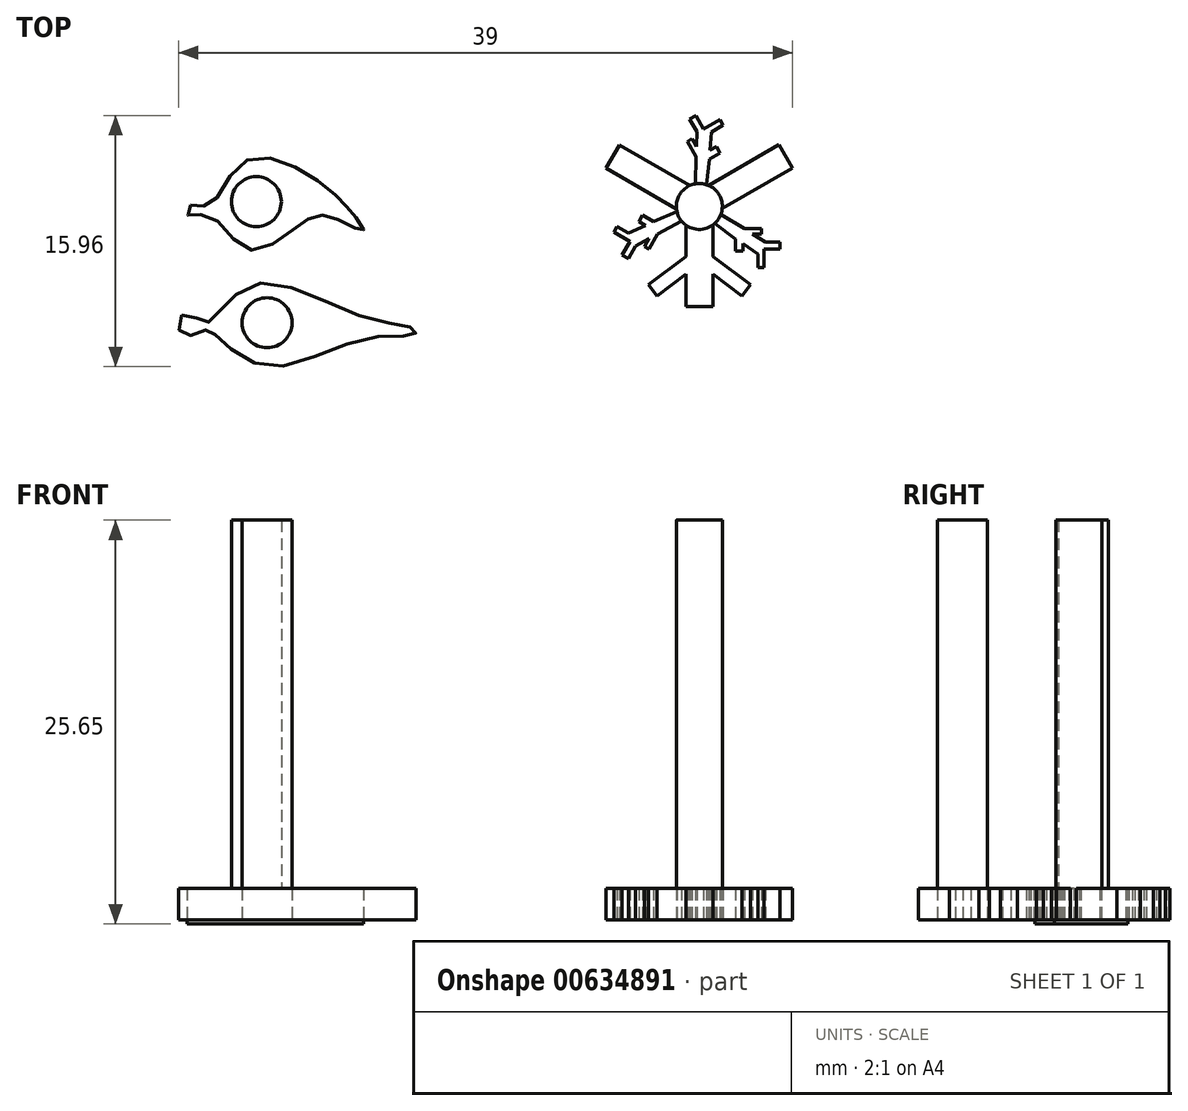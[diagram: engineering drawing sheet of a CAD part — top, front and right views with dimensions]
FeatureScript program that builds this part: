
annotation { "Feature Type Name" : "Feature", "Feature Type Description" : "" }
export const myFeature = defineFeature(function(context is Context, id is Id, definition is map)
    precondition{}
    {
        {
            var Q0;
            Q0=qCreatedBy(makeId("Top.planeOp"),FACE);
            var sketch = newSketch(context, id + "F0", { "sketchPlane" : qUnion([Q0])});
            skLineSegment(sketch, "E0.bottom", {"start": v(-0.85, 0) * mm, "end": v(0.86, 0) * mm});
            skLineSegment(sketch, "E0.top", {"start": v(-0.85, -6.35) * mm, "end": v(0.86, -6.35) * mm});
            skLineSegment(sketch, "E0.left", {"start": v(-0.85, 0) * mm, "end": v(-0.85, -6.35) * mm});
            skLineSegment(sketch, "E0.right", {"start": v(0.86, 0) * mm, "end": v(0.86, -6.35) * mm});
            skLineSegment(sketch, "E1", {"start": v(-0.85, -3.17) * mm, "end": v(-3.24, -4.96) * mm});
            skLineSegment(sketch, "E2", {"start": v(-3.24, -4.96) * mm, "end": v(-2.7, -5.69) * mm});
            skLineSegment(sketch, "E3", {"start": v(-2.7, -5.69) * mm, "end": v(-0.85, -4.3) * mm});
            skLineSegment(sketch, "E4", {"start": v(-0.85, -4.3) * mm, "end": v(-0.85, -3.17) * mm});
            skLineSegment(sketch, "E5", {"start": v(0, 0) * mm, "end": v(0, -6.35) * mm, "construction": true});
            skLineSegment(sketch, "E6.MirrorCS", {"start": v(2.71, -5.69) * mm, "end": v(0.86, -4.3) * mm});
            skLineSegment(sketch, "E7.MirrorCS", {"start": v(3.25, -4.96) * mm, "end": v(2.71, -5.69) * mm});
            skLineSegment(sketch, "E8.MirrorCS", {"start": v(0.86, -3.17) * mm, "end": v(3.25, -4.96) * mm});
            skLineSegment(sketch, "E9.MirrorCS", {"start": v(0.86, -4.3) * mm, "end": v(0.86, -3.17) * mm});
            skLineSegment(sketch, "E10.MirrorCS", {"start": v(0.86, 0) * mm, "end": v(-0.85, 0) * mm});
            skLineSegment(sketch, "E11.MirrorCS", {"start": v(0.86, -6.35) * mm, "end": v(-0.85, -6.35) * mm});
            skLineSegment(sketch, "E12", {"start": v(-0.45, 0) * mm, "end": v(2.29, -2.06) * mm});
            skLineSegment(sketch, "E13", {"start": v(2.29, -2.06) * mm, "end": v(2.29, -2.84) * mm});
            skLineSegment(sketch, "E14", {"start": v(2.29, -2.84) * mm, "end": v(2.76, -2.84) * mm});
            skLineSegment(sketch, "E15", {"start": v(2.76, -2.84) * mm, "end": v(2.76, -2.37) * mm});
            skLineSegment(sketch, "E16", {"start": v(2.76, -2.37) * mm, "end": v(3.71, -3.03) * mm});
            skLineSegment(sketch, "E17", {"start": v(3.71, -3.03) * mm, "end": v(3.71, -3.9) * mm});
            skLineSegment(sketch, "E18", {"start": v(3.71, -3.9) * mm, "end": v(4.12, -3.9) * mm});
            skLineSegment(sketch, "E19", {"start": v(4.12, -3.9) * mm, "end": v(4.12, -2.7) * mm});
            skLineSegment(sketch, "E20", {"start": v(4.12, -2.7) * mm, "end": v(5.12, -2.7) * mm});
            skLineSegment(sketch, "E21", {"start": v(5.12, -2.7) * mm, "end": v(5.12, -2.25) * mm});
            skLineSegment(sketch, "E22", {"start": v(5.12, -2.25) * mm, "end": v(4.2, -2.25) * mm});
            skLineSegment(sketch, "E23", {"start": v(4.2, -2.25) * mm, "end": v(3.38, -1.75) * mm});
            skLineSegment(sketch, "E24", {"start": v(3.38, -1.75) * mm, "end": v(3.95, -1.75) * mm});
            skLineSegment(sketch, "E25", {"start": v(3.95, -1.75) * mm, "end": v(3.95, -1.41) * mm});
            skLineSegment(sketch, "E26", {"start": v(3.95, -1.41) * mm, "end": v(2.86, -1.41) * mm});
            skLineSegment(sketch, "E27", {"start": v(2.86, -1.41) * mm, "end": v(0.5, 0) * mm});
            skLineSegment(sketch, "E28", {"start": v(0.5, 0) * mm, "end": v(-0.45, 0) * mm});
            skLineSegment(sketch, "E29.1.0", {"start": v(-0.75, 4.13) * mm, "end": v(-0.2, 3.18) * mm});
            skLineSegment(sketch, "E29.1.1", {"start": v(2.32, 2.34) * mm, "end": v(2.67, 5.3) * mm});
            skLineSegment(sketch, "E29.1.2", {"start": v(0, 0) * mm, "end": v(5.5, 3.18) * mm, "construction": true});
            skLineSegment(sketch, "E29.1.3", {"start": v(0.43, -0.74) * mm, "end": v(5.92, 2.44) * mm});
            skLineSegment(sketch, "E29.1.4", {"start": v(0.67, 3.57) * mm, "end": v(0.77, 4.73) * mm});
            skLineSegment(sketch, "E29.1.5", {"start": v(-0.61, 5.56) * mm, "end": v(-0.15, 4.75) * mm});
            skLineSegment(sketch, "E29.1.6", {"start": v(3.57, 5.2) * mm, "end": v(3.3, 2.9) * mm});
            skLineSegment(sketch, "E29.1.7", {"start": v(-0.43, 0.75) * mm, "end": v(5.07, 3.92) * mm});
            skLineSegment(sketch, "E29.1.8", {"start": v(3.3, 2.9) * mm, "end": v(2.32, 2.34) * mm});
            skLineSegment(sketch, "E29.1.9", {"start": v(-0.15, 4.75) * mm, "end": v(-0.18, 3.8) * mm});
            skLineSegment(sketch, "E29.1.10", {"start": v(0.28, 4.92) * mm, "end": v(-0.22, 5.78) * mm});
            skLineSegment(sketch, "E29.1.11", {"start": v(5.92, -0.33) * mm, "end": v(6.27, 0.5) * mm});
            skLineSegment(sketch, "E29.1.12", {"start": v(0.77, 4.73) * mm, "end": v(1.51, 5.16) * mm});
            skLineSegment(sketch, "E29.1.13", {"start": v(0.64, 3) * mm, "end": v(1.32, 3.4) * mm});
            skLineSegment(sketch, "E29.1.14", {"start": v(2.67, 5.3) * mm, "end": v(3.57, 5.2) * mm});
            skLineSegment(sketch, "E29.1.15", {"start": v(6.27, 0.5) * mm, "end": v(4.15, 1.41) * mm});
            skLineSegment(sketch, "E29.1.16", {"start": v(-0.2, 3.18) * mm, "end": v(-0.25, 0.43) * mm});
            skLineSegment(sketch, "E29.1.17", {"start": v(5.92, 2.44) * mm, "end": v(5.07, 3.92) * mm});
            skLineSegment(sketch, "E29.1.18", {"start": v(1.3, 5.51) * mm, "end": v(0.28, 4.92) * mm});
            skLineSegment(sketch, "E29.1.19", {"start": v(3.18, 0.85) * mm, "end": v(5.92, -0.33) * mm});
            skLineSegment(sketch, "E29.1.20", {"start": v(0.23, -0.4) * mm, "end": v(0.64, 3) * mm});
            skLineSegment(sketch, "E29.1.21", {"start": v(2.32, 2.34) * mm, "end": v(2.67, 5.3) * mm});
            skLineSegment(sketch, "E29.1.22", {"start": v(2.67, 5.3) * mm, "end": v(3.57, 5.2) * mm});
            skLineSegment(sketch, "E29.1.23", {"start": v(-0.43, 0.75) * mm, "end": v(5.07, 3.92) * mm});
            skLineSegment(sketch, "E29.1.24", {"start": v(0.43, -0.74) * mm, "end": v(5.92, 2.44) * mm});
            skLineSegment(sketch, "E29.1.25", {"start": v(6.27, 0.5) * mm, "end": v(4.15, 1.41) * mm});
            skLineSegment(sketch, "E29.1.26", {"start": v(5.07, 3.92) * mm, "end": v(5.92, 2.44) * mm});
            skLineSegment(sketch, "E29.1.27", {"start": v(5.92, -0.33) * mm, "end": v(6.27, 0.5) * mm});
            skLineSegment(sketch, "E29.1.28", {"start": v(4.15, 1.41) * mm, "end": v(3.18, 0.85) * mm});
            skLineSegment(sketch, "E29.1.29", {"start": v(3.57, 5.2) * mm, "end": v(3.3, 2.9) * mm});
            skLineSegment(sketch, "E29.1.30", {"start": v(-0.25, 0.43) * mm, "end": v(0.23, -0.4) * mm});
            skLineSegment(sketch, "E29.1.31", {"start": v(3.3, 2.9) * mm, "end": v(2.32, 2.34) * mm});
            skLineSegment(sketch, "E29.1.32", {"start": v(3.18, 0.85) * mm, "end": v(5.92, -0.33) * mm});
            skLineSegment(sketch, "E29.1.33", {"start": v(-0.18, 3.8) * mm, "end": v(-0.46, 4.3) * mm});
            skLineSegment(sketch, "E29.1.34", {"start": v(4.15, 1.41) * mm, "end": v(3.18, 0.85) * mm});
            skLineSegment(sketch, "E29.1.35", {"start": v(1.51, 5.16) * mm, "end": v(1.3, 5.51) * mm});
            skLineSegment(sketch, "E29.1.36", {"start": v(-0.22, 5.78) * mm, "end": v(-0.61, 5.56) * mm});
            skLineSegment(sketch, "E29.1.37", {"start": v(1.08, 3.81) * mm, "end": v(0.67, 3.57) * mm});
            skLineSegment(sketch, "E29.1.38", {"start": v(0.43, -0.74) * mm, "end": v(-0.43, 0.75) * mm});
            skLineSegment(sketch, "E29.1.39", {"start": v(-0.46, 4.3) * mm, "end": v(-0.75, 4.13) * mm});
            skLineSegment(sketch, "E29.1.40", {"start": v(1.32, 3.4) * mm, "end": v(1.08, 3.81) * mm});
            skLineSegment(sketch, "E29.1.41", {"start": v(-0.43, 0.75) * mm, "end": v(0.43, -0.74) * mm});
            skLineSegment(sketch, "E29.2.0", {"start": v(-3.2, -2.72) * mm, "end": v(-2.65, -1.77) * mm});
            skLineSegment(sketch, "E29.2.1", {"start": v(-3.18, 0.84) * mm, "end": v(-5.93, -0.34) * mm});
            skLineSegment(sketch, "E29.2.2", {"start": v(0, 0) * mm, "end": v(-5.5, 3.17) * mm, "construction": true});
            skLineSegment(sketch, "E29.2.3", {"start": v(0.43, 0.74) * mm, "end": v(-5.07, 3.91) * mm});
            skLineSegment(sketch, "E29.2.4", {"start": v(-3.43, -1.2) * mm, "end": v(-4.48, -1.7) * mm});
            skLineSegment(sketch, "E29.2.5", {"start": v(-4.5, -3.3) * mm, "end": v(-4.04, -2.5) * mm});
            skLineSegment(sketch, "E29.2.6", {"start": v(-6.28, 0.5) * mm, "end": v(-4.16, 1.4) * mm});
            skLineSegment(sketch, "E29.2.7", {"start": v(-0.43, -0.75) * mm, "end": v(-5.93, 2.43) * mm});
            skLineSegment(sketch, "E29.2.8", {"start": v(-4.16, 1.4) * mm, "end": v(-3.18, 0.84) * mm});
            skLineSegment(sketch, "E29.2.9", {"start": v(-4.04, -2.5) * mm, "end": v(-3.2, -2.05) * mm});
            skLineSegment(sketch, "E29.2.10", {"start": v(-4.4, -2.22) * mm, "end": v(-4.9, -3.08) * mm});
            skLineSegment(sketch, "E29.2.11", {"start": v(-2.68, 5.29) * mm, "end": v(-3.57, 5.18) * mm});
            skLineSegment(sketch, "E29.2.12", {"start": v(-4.48, -1.7) * mm, "end": v(-5.23, -1.27) * mm});
            skLineSegment(sketch, "E29.2.13", {"start": v(-2.92, -0.95) * mm, "end": v(-3.6, -0.56) * mm});
            skLineSegment(sketch, "E29.2.14", {"start": v(-5.93, -0.34) * mm, "end": v(-6.28, 0.5) * mm});
            skLineSegment(sketch, "E29.2.15", {"start": v(-3.57, 5.18) * mm, "end": v(-3.3, 2.89) * mm});
            skLineSegment(sketch, "E29.2.16", {"start": v(-2.65, -1.77) * mm, "end": v(-0.25, -0.43) * mm});
            skLineSegment(sketch, "E29.2.17", {"start": v(-5.07, 3.91) * mm, "end": v(-5.93, 2.43) * mm});
            skLineSegment(sketch, "E29.2.18", {"start": v(-5.43, -1.62) * mm, "end": v(-4.4, -2.22) * mm});
            skLineSegment(sketch, "E29.2.19", {"start": v(-2.32, 2.32) * mm, "end": v(-2.68, 5.29) * mm});
            skLineSegment(sketch, "E29.2.20", {"start": v(0.23, 0.4) * mm, "end": v(-2.92, -0.95) * mm});
            skLineSegment(sketch, "E29.2.21", {"start": v(-3.18, 0.84) * mm, "end": v(-5.93, -0.34) * mm});
            skLineSegment(sketch, "E29.2.22", {"start": v(-5.93, -0.34) * mm, "end": v(-6.28, 0.5) * mm});
            skLineSegment(sketch, "E29.2.23", {"start": v(-0.43, -0.75) * mm, "end": v(-5.93, 2.43) * mm});
            skLineSegment(sketch, "E29.2.24", {"start": v(0.43, 0.74) * mm, "end": v(-5.07, 3.91) * mm});
            skLineSegment(sketch, "E29.2.25", {"start": v(-3.57, 5.18) * mm, "end": v(-3.3, 2.89) * mm});
            skLineSegment(sketch, "E29.2.26", {"start": v(-5.93, 2.43) * mm, "end": v(-5.07, 3.91) * mm});
            skLineSegment(sketch, "E29.2.27", {"start": v(-2.68, 5.29) * mm, "end": v(-3.57, 5.18) * mm});
            skLineSegment(sketch, "E29.2.28", {"start": v(-3.3, 2.89) * mm, "end": v(-2.32, 2.32) * mm});
            skLineSegment(sketch, "E29.2.29", {"start": v(-6.28, 0.5) * mm, "end": v(-4.16, 1.4) * mm});
            skLineSegment(sketch, "E29.2.30", {"start": v(-0.25, -0.43) * mm, "end": v(0.23, 0.4) * mm});
            skLineSegment(sketch, "E29.2.31", {"start": v(-4.16, 1.4) * mm, "end": v(-3.18, 0.84) * mm});
            skLineSegment(sketch, "E29.2.32", {"start": v(-2.32, 2.32) * mm, "end": v(-2.68, 5.29) * mm});
            skLineSegment(sketch, "E29.2.33", {"start": v(-3.2, -2.05) * mm, "end": v(-3.49, -2.55) * mm});
            skLineSegment(sketch, "E29.2.34", {"start": v(-3.3, 2.89) * mm, "end": v(-2.32, 2.32) * mm});
            skLineSegment(sketch, "E29.2.35", {"start": v(-5.23, -1.27) * mm, "end": v(-5.43, -1.62) * mm});
            skLineSegment(sketch, "E29.2.36", {"start": v(-4.9, -3.08) * mm, "end": v(-4.5, -3.3) * mm});
            skLineSegment(sketch, "E29.2.37", {"start": v(-3.84, -0.97) * mm, "end": v(-3.43, -1.2) * mm});
            skLineSegment(sketch, "E29.2.38", {"start": v(0.43, 0.74) * mm, "end": v(-0.43, -0.75) * mm});
            skLineSegment(sketch, "E29.2.39", {"start": v(-3.49, -2.55) * mm, "end": v(-3.2, -2.72) * mm});
            skLineSegment(sketch, "E29.2.40", {"start": v(-3.6, -0.56) * mm, "end": v(-3.84, -0.97) * mm});
            skLineSegment(sketch, "E29.2.41", {"start": v(-0.43, -0.75) * mm, "end": v(0.43, 0.74) * mm});
            skPoint(sketch, "E29.center", {"position": v(0, 0) * mm});
            skSolve(sketch);
        }
        {
            var Q0;
            Q0=qCreatedBy(makeId("Top.planeOp"),FACE);
            var sketch = newSketch(context, id + "F1", { "sketchPlane" : qUnion([Q0])});
            skCircle(sketch, "E30", {"center": v(0, 0) * mm, "radius": 1.46 * mm});
            skSolve(sketch);
        }
        {
            var Q0;
            {var subQ9=sQuery(id+"F0.wireOp",EDGE,"032354c9-7b22-4bc2-b53b-3968bda45a61.1.0");Q0=makeQuery(id+"F0.imprint","IMPRINT",FACE,{"disambiguationData":[TD([[makeQuery(id+"F0.imprint","IMPRINT",EDGE,{"derivedFrom":subQ9}),1.0]])]});}
            var Q1;
            {var subQ9=sQuery(id+"F0.wireOp",EDGE,"032354c9-7b22-4bc2-b53b-3968bda45a61.2.0");Q1=makeQuery(id+"F0.imprint","IMPRINT",FACE,{"disambiguationData":[TD([[makeQuery(id+"F0.imprint","IMPRINT",EDGE,{"derivedFrom":subQ9}),1.0]])]});}
            var Q2;
            {var subQ8=sQuery(id+"F0.wireOp",EDGE,"032354c9-7b22-4bc2-b53b-3968bda45a61.1.30");Q2=makeQuery(id+"F0.imprint","IMPRINT",FACE,{"disambiguationData":[TD([[makeQuery(id+"F0.imprint","IMPRINT",EDGE,{"derivedFrom":subQ8}),-1.0]])]});}
            var Q3;
            {var subQ10=sQuery(id+"F0.wireOp",EDGE,"E11.MirrorCS");Q3=makeQuery(id+"F0.imprint","IMPRINT",FACE,{"disambiguationData":[TD([[makeQuery(id+"F0.imprint","IMPRINT",EDGE,{"derivedFrom":subQ10}),-1.0]])]});}
            var Q4;
            {var subQ0=sQuery(id+"F0.wireOp",EDGE,"E1");Q4=makeQuery(id+"F0.imprint","IMPRINT",FACE,{"disambiguationData":[TD([[makeQuery(id+"F0.imprint","IMPRINT",EDGE,{"derivedFrom":subQ0}),1.0]])]});}
            var Q5;
            Q5=makeQuery(id+"F0.imprint","IMPRINT",FACE,{"disambiguationData":[TD([[makeQuery(id+"F0.imprint","IMPRINT",EDGE,{"derivedFrom":sQuery(id+"F0.wireOp",EDGE,"E8.MirrorCS")}),-1.0]])]});
            var Q6;
            {var subQ0=sQuery(id+"F0.wireOp",EDGE,"D4slwSDG-l3qi-5vr4-5RfH-pFX6ATX0QrVD");Q6=makeQuery(id+"F0.imprint","IMPRINT",FACE,{"disambiguationData":[TD([[makeQuery(id+"F0.imprint","IMPRINT",EDGE,{"derivedFrom":subQ0}),1.0]])]});}
            var Q7;
            {var subQ1=sQuery(id+"F0.wireOp",EDGE,"98ac017a-216a-4e28-945e-33d32b6503b70.MirrorCS");Q7=makeQuery(id+"F0.imprint","IMPRINT",FACE,{"disambiguationData":[TD([[makeQuery(id+"F0.imprint","IMPRINT",EDGE,{"derivedFrom":subQ1}),-1.0]])]});}
            var Q8;
            {var subQ0=sQuery(id+"F0.wireOp",EDGE,"032354c9-7b22-4bc2-b53b-3968bda45a61.1.3");Q8=makeQuery(id+"F0.imprint","IMPRINT",FACE,{"disambiguationData":[TD([[makeQuery(id+"F0.imprint","IMPRINT",EDGE,{"derivedFrom":subQ0}),1.0]])]});}
            var Q9;
            {var subQ1=sQuery(id+"F0.wireOp",EDGE,"032354c9-7b22-4bc2-b53b-3968bda45a61.1.10");Q9=makeQuery(id+"F0.imprint","IMPRINT",FACE,{"disambiguationData":[TD([[makeQuery(id+"F0.imprint","IMPRINT",EDGE,{"derivedFrom":subQ1}),-1.0]])]});}
            var Q10;
            Q10=makeQuery(id+"F0.imprint","IMPRINT",FACE,{"disambiguationData":[TD([[makeQuery(id+"F0.imprint","IMPRINT",EDGE,{"derivedFrom":sQuery(id+"F0.wireOp",EDGE,"032354c9-7b22-4bc2-b53b-3968bda45a61.1.23")}),1.0]])]});
            var Q11;
            Q11=makeQuery(id+"F0.imprint","IMPRINT",FACE,{"disambiguationData":[TD([[makeQuery(id+"F0.imprint","IMPRINT",EDGE,{"derivedFrom":sQuery(id+"F0.wireOp",EDGE,"032354c9-7b22-4bc2-b53b-3968bda45a61.1.24")}),-1.0]])]});
            var Q12;
            {var subQ0=sQuery(id+"F0.wireOp",EDGE,"032354c9-7b22-4bc2-b53b-3968bda45a61.2.3");Q12=makeQuery(id+"F0.imprint","IMPRINT",FACE,{"disambiguationData":[TD([[makeQuery(id+"F0.imprint","IMPRINT",EDGE,{"derivedFrom":subQ0}),1.0]])]});}
            var Q13;
            {var subQ1=sQuery(id+"F0.wireOp",EDGE,"032354c9-7b22-4bc2-b53b-3968bda45a61.2.10");Q13=makeQuery(id+"F0.imprint","IMPRINT",FACE,{"disambiguationData":[TD([[makeQuery(id+"F0.imprint","IMPRINT",EDGE,{"derivedFrom":subQ1}),-1.0]])]});}
            var Q14;
            Q14=makeQuery(id+"F0.imprint","IMPRINT",FACE,{"disambiguationData":[TD([[makeQuery(id+"F0.imprint","IMPRINT",EDGE,{"derivedFrom":sQuery(id+"F0.wireOp",EDGE,"032354c9-7b22-4bc2-b53b-3968bda45a61.2.23")}),1.0]])]});
            var Q15;
            Q15=makeQuery(id+"F0.imprint","IMPRINT",FACE,{"disambiguationData":[TD([[makeQuery(id+"F0.imprint","IMPRINT",EDGE,{"derivedFrom":sQuery(id+"F0.wireOp",EDGE,"032354c9-7b22-4bc2-b53b-3968bda45a61.2.24")}),-1.0]])]});
            var Q16;
            {var subQ1=sQuery(id+"F0.wireOp",EDGE,"E10.MirrorCS");var subQ3=sQuery(id+"F0.wireOp",EDGE,"vSjqWOQx-EUP5-Ulzc-yrVZ-XqxAPtUXXuhp");var subQ4=makeQuery(id+"F0.imprint","INTERSECT",VERTEX,{"derivedFrom":[subQ1,subQ3]});Q16=makeQuery(id+"F0.imprint","IMPRINT",FACE,{"disambiguationData":[TD([[makeQuery(id+"F0.imprint","IMPRINT",EDGE,{"disambiguationData":[TD([[subQ4,-1.0]])],"derivedFrom":subQ3}),1.0]])]});}
            var Q17;
            {var subQ2=sQuery(id+"F0.wireOp",EDGE,"032354c9-7b22-4bc2-b53b-3968bda45a61.2.30");Q17=makeQuery(id+"F0.imprint","IMPRINT",FACE,{"disambiguationData":[TD([[makeQuery(id+"F0.imprint","IMPRINT",EDGE,{"derivedFrom":subQ2}),-1.0]])]});}
            var Q18;
            {var subQ6=sQuery(id+"F0.wireOp",EDGE,"NORLGcSs-udQc-MrU3-SgNm-p8DdZcNEeP8l");Q18=makeQuery(id+"F0.imprint","IMPRINT",FACE,{"disambiguationData":[TD([[makeQuery(id+"F0.imprint","IMPRINT",EDGE,{"derivedFrom":subQ6}),1.0]])]});}
            var Q19;
            {var subQ0=sQuery(id+"F0.wireOp",EDGE,"vSjqWOQx-EUP5-Ulzc-yrVZ-XqxAPtUXXuhp");var subQ1=sQuery(id+"F0.wireOp",EDGE,"E10.MirrorCS");var subQ2=makeQuery(id+"F0.imprint","INTERSECT",VERTEX,{"derivedFrom":[subQ1,subQ0]});Q19=makeQuery(id+"F0.imprint","IMPRINT",FACE,{"disambiguationData":[TD([[makeQuery(id+"F0.imprint","IMPRINT",EDGE,{"disambiguationData":[TD([[subQ2,-1.0]])],"derivedFrom":subQ0}),-1.0]])]});}
            var Q20;
            {var subQ0=sQuery(id+"F0.wireOp",EDGE,"032354c9-7b22-4bc2-b53b-3968bda45a61.1.28");var subQ1=sQuery(id+"F0.wireOp",EDGE,"032354c9-7b22-4bc2-b53b-3968bda45a61.1.8");var subQ2=makeQuery(id+"F0.imprint","INTERSECT",VERTEX,{"derivedFrom":[subQ1,subQ0]});Q20=makeQuery(id+"F0.imprint","IMPRINT",FACE,{"disambiguationData":[TD([[makeQuery(id+"F0.imprint","IMPRINT",EDGE,{"disambiguationData":[TD([[subQ2,-1.0]])],"derivedFrom":subQ1}),1.0]])]});}
            var Q21;
            {var subQ0=sQuery(id+"F0.wireOp",EDGE,"032354c9-7b22-4bc2-b53b-3968bda45a61.1.28");var subQ1=sQuery(id+"F0.wireOp",EDGE,"032354c9-7b22-4bc2-b53b-3968bda45a61.1.8");var subQ2=makeQuery(id+"F0.imprint","INTERSECT",VERTEX,{"derivedFrom":[subQ1,subQ0]});Q21=makeQuery(id+"F0.imprint","IMPRINT",FACE,{"disambiguationData":[TD([[makeQuery(id+"F0.imprint","IMPRINT",EDGE,{"disambiguationData":[TD([[subQ2,-1.0]])],"derivedFrom":subQ1}),-1.0]])]});}
            var Q22;
            {var subQ0=sQuery(id+"F0.wireOp",EDGE,"032354c9-7b22-4bc2-b53b-3968bda45a61.2.8");var subQ1=sQuery(id+"F0.wireOp",EDGE,"E0.left");var subQ2=makeQuery(id+"F0.imprint","INTERSECT",VERTEX,{"derivedFrom":[subQ1,subQ0]});Q22=makeQuery(id+"F0.imprint","IMPRINT",FACE,{"disambiguationData":[TD([[makeQuery(id+"F0.imprint","IMPRINT",EDGE,{"disambiguationData":[TD([[subQ2,-1.0]])],"derivedFrom":subQ1}),1.0]])]});}
            var Q23;
            {var subQ0=sQuery(id+"F0.wireOp",EDGE,"E0.left");var subQ1=sQuery(id+"F0.wireOp",EDGE,"E10.MirrorCS");var subQ2=makeQuery(id+"F0.imprint","INTERSECT",VERTEX,{"derivedFrom":[subQ1,subQ0]});Q23=makeQuery(id+"F0.imprint","IMPRINT",FACE,{"disambiguationData":[TD([[makeQuery(id+"F0.imprint","IMPRINT",EDGE,{"disambiguationData":[TD([[subQ2,-1.0]])],"derivedFrom":subQ0}),1.0]])]});}
            var Q24;
            {var subQ0=sQuery(id+"F0.wireOp",EDGE,"LsFTkbss-DpKE-GpSw-1EOr-DqLiLPciGQV8");var subQ3=sQuery(id+"F0.wireOp",EDGE,"032354c9-7b22-4bc2-b53b-3968bda45a61.1.34");var subQ5=makeQuery(id+"F0.imprint","INTERSECT",VERTEX,{"derivedFrom":[subQ0,subQ3]});Q24=makeQuery(id+"F0.imprint","IMPRINT",FACE,{"disambiguationData":[TD([[makeQuery(id+"F0.imprint","IMPRINT",EDGE,{"disambiguationData":[TD([[subQ5,1.0]])],"derivedFrom":subQ3}),1.0]])]});}
            var Q25;
            {var subQ0=sQuery(id+"F0.wireOp",EDGE,"032354c9-7b22-4bc2-b53b-3968bda45a61.2.16");var subQ1=sQuery(id+"F0.wireOp",EDGE,"E0.left");var subQ2=makeQuery(id+"F0.imprint","INTERSECT",VERTEX,{"derivedFrom":[subQ1,subQ0]});Q25=makeQuery(id+"F0.imprint","IMPRINT",FACE,{"disambiguationData":[TD([[makeQuery(id+"F0.imprint","IMPRINT",EDGE,{"disambiguationData":[TD([[subQ2,1.0]])],"derivedFrom":subQ1}),1.0]])]});}
            var Q26;
            {var subQ0=sQuery(id+"F0.wireOp",EDGE,"032354c9-7b22-4bc2-b53b-3968bda45a61.1.31");var subQ1=sQuery(id+"F0.wireOp",EDGE,"032354c9-7b22-4bc2-b53b-3968bda45a61.1.8");var subQ2=makeQuery(id+"F0.imprint","INTERSECT",VERTEX,{"derivedFrom":[subQ1,subQ0]});Q26=makeQuery(id+"F0.imprint","IMPRINT",FACE,{"disambiguationData":[TD([[makeQuery(id+"F0.imprint","IMPRINT",EDGE,{"disambiguationData":[TD([[subQ2,1.0]])],"derivedFrom":subQ1}),1.0]])]});}
            var Q27;
            {var subQ0=sQuery(id+"F0.wireOp",EDGE,"032354c9-7b22-4bc2-b53b-3968bda45a61.2.8");var subQ1=sQuery(id+"F0.wireOp",EDGE,"E0.left");var subQ2=makeQuery(id+"F0.imprint","INTERSECT",VERTEX,{"derivedFrom":[subQ1,subQ0]});Q27=makeQuery(id+"F0.imprint","IMPRINT",FACE,{"disambiguationData":[TD([[makeQuery(id+"F0.imprint","IMPRINT",EDGE,{"disambiguationData":[TD([[subQ2,-1.0]])],"derivedFrom":subQ1}),-1.0]])]});}
            var Q28;
            {var subQ0=sQuery(id+"F0.wireOp",EDGE,"032354c9-7b22-4bc2-b53b-3968bda45a61.1.37");var subQ1=sQuery(id+"F0.wireOp",EDGE,"032354c9-7b22-4bc2-b53b-3968bda45a61.1.6");var subQ2=makeQuery(id+"F0.imprint","INTERSECT",VERTEX,{"derivedFrom":[subQ1,subQ0]});Q28=makeQuery(id+"F0.imprint","IMPRINT",FACE,{"disambiguationData":[TD([[makeQuery(id+"F0.imprint","IMPRINT",EDGE,{"disambiguationData":[TD([[subQ2,1.0]])],"derivedFrom":subQ1}),-1.0]])]});}
            var Q29;
            {var subQ0=sQuery(id+"F0.wireOp",EDGE,"1507031a-2216-419c-b823-908dcabe06120.MirrorCS");var subQ1=sQuery(id+"F0.wireOp",EDGE,"LsFTkbss-DpKE-GpSw-1EOr-DqLiLPciGQV8");var subQ2=makeQuery(id+"F0.imprint","INTERSECT",VERTEX,{"derivedFrom":[subQ1,subQ0]});Q29=makeQuery(id+"F0.imprint","IMPRINT",FACE,{"disambiguationData":[TD([[makeQuery(id+"F0.imprint","IMPRINT",EDGE,{"disambiguationData":[TD([[subQ2,-1.0]])],"derivedFrom":subQ1}),1.0]])]});}
            var Q30;
            {var subQ1=sQuery(id+"F0.wireOp",EDGE,"032354c9-7b22-4bc2-b53b-3968bda45a61.1.16");var subQ3=sQuery(id+"F0.wireOp",EDGE,"032354c9-7b22-4bc2-b53b-3968bda45a61.2.34");var subQ4=makeQuery(id+"F0.imprint","INTERSECT",VERTEX,{"derivedFrom":[subQ1,subQ3]});Q30=makeQuery(id+"F0.imprint","IMPRINT",FACE,{"disambiguationData":[TD([[makeQuery(id+"F0.imprint","IMPRINT",EDGE,{"disambiguationData":[TD([[subQ4,1.0]])],"derivedFrom":subQ3}),1.0]])]});}
            var Q31;
            {var subQ0=sQuery(id+"F0.wireOp",EDGE,"vSjqWOQx-EUP5-Ulzc-yrVZ-XqxAPtUXXuhp");var subQ1=sQuery(id+"F0.wireOp",EDGE,"E0.right");var subQ2=makeQuery(id+"F0.imprint","INTERSECT",VERTEX,{"derivedFrom":[subQ1,subQ0]});Q31=makeQuery(id+"F0.imprint","IMPRINT",FACE,{"disambiguationData":[TD([[makeQuery(id+"F0.imprint","IMPRINT",EDGE,{"disambiguationData":[TD([[subQ2,1.0]])],"derivedFrom":subQ1}),-1.0]])]});}
            var Q32;
            {var subQ0=sQuery(id+"F0.wireOp",EDGE,"032354c9-7b22-4bc2-b53b-3968bda45a61.2.37");var subQ1=sQuery(id+"F0.wireOp",EDGE,"032354c9-7b22-4bc2-b53b-3968bda45a61.2.6");var subQ2=makeQuery(id+"F0.imprint","INTERSECT",VERTEX,{"derivedFrom":[subQ1,subQ0]});Q32=makeQuery(id+"F0.imprint","IMPRINT",FACE,{"disambiguationData":[TD([[makeQuery(id+"F0.imprint","IMPRINT",EDGE,{"disambiguationData":[TD([[subQ2,1.0]])],"derivedFrom":subQ1}),-1.0]])]});}
            var Q33;
            {var subQ0=sQuery(id+"F0.wireOp",EDGE,"E29.2.26");Q33=makeQuery(id+"F0.imprint","IMPRINT",FACE,{"disambiguationData":[TD([[makeQuery(id+"F0.imprint","IMPRINT",EDGE,{"derivedFrom":subQ0}),-1.0]])]});}
            var Q34;
            {var subQ1=sQuery(id+"F0.wireOp",EDGE,"E29.2.0");Q34=makeQuery(id+"F0.imprint","IMPRINT",FACE,{"disambiguationData":[TD([[makeQuery(id+"F0.imprint","IMPRINT",EDGE,{"derivedFrom":subQ1}),1.0]])]});}
            var Q35;
            Q35=makeQuery(id+"F0.imprint","IMPRINT",FACE,{"disambiguationData":[TD([[makeQuery(id+"F0.imprint","IMPRINT",EDGE,{"derivedFrom":sQuery(id+"F0.wireOp",EDGE,"E29.2.21")}),-1.0]])]});
            var Q36;
            Q36=makeQuery(id+"F0.imprint","IMPRINT",FACE,{"disambiguationData":[TD([[makeQuery(id+"F0.imprint","IMPRINT",EDGE,{"derivedFrom":sQuery(id+"F0.wireOp",EDGE,"E29.2.25")}),1.0]])]});
            var Q37;
            {var subQ1=sQuery(id+"F0.wireOp",EDGE,"E29.1.0");Q37=makeQuery(id+"F0.imprint","IMPRINT",FACE,{"disambiguationData":[TD([[makeQuery(id+"F0.imprint","IMPRINT",EDGE,{"derivedFrom":subQ1}),1.0]])]});}
            var Q38;
            Q38=makeQuery(id+"F0.imprint","IMPRINT",FACE,{"disambiguationData":[TD([[makeQuery(id+"F0.imprint","IMPRINT",EDGE,{"derivedFrom":sQuery(id+"F0.wireOp",EDGE,"E29.1.21")}),-1.0]])]});
            var Q39;
            {var subQ0=sQuery(id+"F0.wireOp",EDGE,"E29.1.26");Q39=makeQuery(id+"F0.imprint","IMPRINT",FACE,{"disambiguationData":[TD([[makeQuery(id+"F0.imprint","IMPRINT",EDGE,{"derivedFrom":subQ0}),-1.0]])]});}
            var Q40;
            Q40=makeQuery(id+"F0.imprint","IMPRINT",FACE,{"disambiguationData":[TD([[makeQuery(id+"F0.imprint","IMPRINT",EDGE,{"derivedFrom":sQuery(id+"F0.wireOp",EDGE,"E29.1.25")}),1.0]])]});
            var Q41;
            {var subQ5=sQuery(id+"F0.wireOp",EDGE,"E13");Q41=makeQuery(id+"F0.imprint","IMPRINT",FACE,{"disambiguationData":[TD([[makeQuery(id+"F0.imprint","IMPRINT",EDGE,{"derivedFrom":subQ5}),1.0]])]});}
            var Q42;
            {var subQ1=sQuery(id+"F0.wireOp",EDGE,"E27");var subQ3=sQuery(id+"F0.wireOp",EDGE,"E0.right");var subQ4=makeQuery(id+"F0.imprint","INTERSECT",VERTEX,{"derivedFrom":[subQ3,subQ1]});Q42=makeQuery(id+"F0.imprint","IMPRINT",FACE,{"disambiguationData":[TD([[makeQuery(id+"F0.imprint","IMPRINT",EDGE,{"disambiguationData":[TD([[subQ4,-1.0]])],"derivedFrom":subQ3}),-1.0]])]});}
            var Q43;
            {var subQ5=sQuery(id+"F0.wireOp",EDGE,"E29.2.20");var subQ6=sQuery(id+"F0.wireOp",EDGE,"E0.left");var subQ7=makeQuery(id+"F0.imprint","INTERSECT",VERTEX,{"derivedFrom":[subQ6,subQ5]});Q43=makeQuery(id+"F0.imprint","IMPRINT",FACE,{"disambiguationData":[TD([[makeQuery(id+"F0.imprint","IMPRINT",EDGE,{"disambiguationData":[TD([[subQ7,-1.0]])],"derivedFrom":subQ6}),1.0]])]});}
            var Q44;
            {var subQ0=sQuery(id+"F0.wireOp",EDGE,"E29.1.41");var subQ1=sQuery(id+"F0.wireOp",EDGE,"E29.1.16");var subQ2=makeQuery(id+"F0.imprint","INTERSECT",VERTEX,{"derivedFrom":[subQ1,subQ0]});Q44=makeQuery(id+"F0.imprint","IMPRINT",FACE,{"disambiguationData":[TD([[makeQuery(id+"F0.imprint","IMPRINT",EDGE,{"disambiguationData":[TD([[subQ2,1.0]])],"derivedFrom":subQ1}),1.0]])]});}
            var Q45;
            {var subQ0=sQuery(id+"F0.wireOp",EDGE,"E29.1.23");var subQ1=sQuery(id+"F0.wireOp",EDGE,"E29.1.20");var subQ2=makeQuery(id+"F0.imprint","INTERSECT",VERTEX,{"derivedFrom":[subQ1,subQ0]});Q45=makeQuery(id+"F0.imprint","IMPRINT",FACE,{"disambiguationData":[TD([[makeQuery(id+"F0.imprint","IMPRINT",EDGE,{"disambiguationData":[TD([[subQ2,1.0]])],"derivedFrom":subQ1}),1.0]])]});}
            var Q46;
            {var subQ0=sQuery(id+"F0.wireOp",EDGE,"E27");var subQ1=sQuery(id+"F0.wireOp",EDGE,"E0.right");var subQ2=makeQuery(id+"F0.imprint","INTERSECT",VERTEX,{"derivedFrom":[subQ1,subQ0]});Q46=makeQuery(id+"F0.imprint","IMPRINT",FACE,{"disambiguationData":[TD([[makeQuery(id+"F0.imprint","IMPRINT",EDGE,{"disambiguationData":[TD([[subQ2,-1.0]])],"derivedFrom":subQ1}),1.0]])]});}
            var Q47;
            {var subQ0=sQuery(id+"F0.wireOp",EDGE,"E29.2.41");var subQ1=sQuery(id+"F0.wireOp",EDGE,"E29.2.16");var subQ2=makeQuery(id+"F0.imprint","INTERSECT",VERTEX,{"derivedFrom":[subQ1,subQ0]});Q47=makeQuery(id+"F0.imprint","IMPRINT",FACE,{"disambiguationData":[TD([[makeQuery(id+"F0.imprint","IMPRINT",EDGE,{"disambiguationData":[TD([[subQ2,1.0]])],"derivedFrom":subQ1}),-1.0]])]});}
            var Q48;
            {var subQ0=sQuery(id+"F0.wireOp",EDGE,"E29.2.16");var subQ1=sQuery(id+"F0.wireOp",EDGE,"E0.left");var subQ2=makeQuery(id+"F0.imprint","INTERSECT",VERTEX,{"derivedFrom":[subQ1,subQ0]});Q48=makeQuery(id+"F0.imprint","IMPRINT",FACE,{"disambiguationData":[TD([[makeQuery(id+"F0.imprint","IMPRINT",EDGE,{"disambiguationData":[TD([[subQ2,1.0]])],"derivedFrom":subQ1}),1.0]])]});}
            var Q49;
            {var subQ0=sQuery(id+"F0.wireOp",EDGE,"E29.1.41");var subQ1=sQuery(id+"F0.wireOp",EDGE,"E29.1.16");var subQ2=makeQuery(id+"F0.imprint","INTERSECT",VERTEX,{"derivedFrom":[subQ1,subQ0]});Q49=makeQuery(id+"F0.imprint","IMPRINT",FACE,{"disambiguationData":[TD([[makeQuery(id+"F0.imprint","IMPRINT",EDGE,{"disambiguationData":[TD([[subQ2,1.0]])],"derivedFrom":subQ1}),-1.0]])]});}
            var Q50;
            {var subQ0=sQuery(id+"F0.wireOp",EDGE,"E29.2.24");var subQ1=sQuery(id+"F0.wireOp",EDGE,"E29.1.16");var subQ2=makeQuery(id+"F0.imprint","INTERSECT",VERTEX,{"derivedFrom":[subQ1,subQ0]});Q50=makeQuery(id+"F0.imprint","IMPRINT",FACE,{"disambiguationData":[TD([[makeQuery(id+"F0.imprint","IMPRINT",EDGE,{"disambiguationData":[TD([[subQ2,-1.0]])],"derivedFrom":subQ1}),1.0]])]});}
            var Q51;
            {var subQ0=sQuery(id+"F0.wireOp",EDGE,"E29.1.20");var subQ1=sQuery(id+"F0.wireOp",EDGE,"E28");var subQ2=makeQuery(id+"F0.imprint","INTERSECT",VERTEX,{"derivedFrom":[subQ1,subQ0]});Q51=makeQuery(id+"F0.imprint","IMPRINT",FACE,{"disambiguationData":[TD([[makeQuery(id+"F0.imprint","IMPRINT",EDGE,{"disambiguationData":[TD([[subQ2,-1.0]])],"derivedFrom":subQ0}),1.0]])]});}
            var Q52;
            {var subQ0=sQuery(id+"F0.wireOp",EDGE,"E29.2.20");var subQ3=sQuery(id+"F0.wireOp",EDGE,"E29.2.41");var subQ5=makeQuery(id+"F0.imprint","INTERSECT",VERTEX,{"derivedFrom":[subQ0,subQ3]});Q52=makeQuery(id+"F0.imprint","IMPRINT",FACE,{"disambiguationData":[TD([[makeQuery(id+"F0.imprint","IMPRINT",EDGE,{"disambiguationData":[TD([[subQ5,-1.0]])],"derivedFrom":subQ0}),1.0]])]});}
            var Q53;
            {var subQ1=sQuery(id+"F0.wireOp",EDGE,"E10.MirrorCS");var subQ3=sQuery(id+"F0.wireOp",EDGE,"E29.2.20");var subQ4=makeQuery(id+"F0.imprint","INTERSECT",VERTEX,{"derivedFrom":[subQ1,subQ3]});Q53=makeQuery(id+"F0.imprint","IMPRINT",FACE,{"disambiguationData":[TD([[makeQuery(id+"F0.imprint","IMPRINT",EDGE,{"disambiguationData":[TD([[subQ4,1.0]])],"derivedFrom":subQ3}),1.0]])]});}
            var Q54;
            {var subQ1=sQuery(id+"F0.wireOp",EDGE,"E12");var subQ3=sQuery(id+"F0.wireOp",EDGE,"E29.2.41");var subQ4=makeQuery(id+"F0.imprint","INTERSECT",VERTEX,{"derivedFrom":[subQ1,subQ3]});Q54=makeQuery(id+"F0.imprint","IMPRINT",FACE,{"disambiguationData":[TD([[makeQuery(id+"F0.imprint","IMPRINT",EDGE,{"disambiguationData":[TD([[subQ4,1.0]])],"derivedFrom":subQ1}),1.0]])]});}
            var Q55;
            {var subQ0=sQuery(id+"F0.wireOp",EDGE,"E29.2.41");var subQ1=sQuery(id+"F0.wireOp",EDGE,"E12");var subQ2=makeQuery(id+"F0.imprint","INTERSECT",VERTEX,{"derivedFrom":[subQ1,subQ0]});Q55=makeQuery(id+"F0.imprint","IMPRINT",FACE,{"disambiguationData":[TD([[makeQuery(id+"F0.imprint","IMPRINT",EDGE,{"disambiguationData":[TD([[subQ2,-1.0]])],"derivedFrom":subQ1}),1.0]])]});}
            var Q56;
            {var subQ0=sQuery(id+"F0.wireOp",EDGE,"E29.1.20");var subQ3=sQuery(id+"F0.wireOp",EDGE,"E29.1.41");var subQ5=makeQuery(id+"F0.imprint","INTERSECT",VERTEX,{"derivedFrom":[subQ0,subQ3]});Q56=makeQuery(id+"F0.imprint","IMPRINT",FACE,{"disambiguationData":[TD([[makeQuery(id+"F0.imprint","IMPRINT",EDGE,{"disambiguationData":[TD([[subQ5,-1.0]])],"derivedFrom":subQ0}),1.0]])]});}
            var Q57;
            {var subQ0=sQuery(id+"F0.wireOp",EDGE,"E29.2.41");var subQ1=sQuery(id+"F0.wireOp",EDGE,"E29.1.20");var subQ2=makeQuery(id+"F0.imprint","INTERSECT",VERTEX,{"derivedFrom":[subQ1,subQ0]});Q57=makeQuery(id+"F0.imprint","IMPRINT",FACE,{"disambiguationData":[TD([[makeQuery(id+"F0.imprint","IMPRINT",EDGE,{"disambiguationData":[TD([[subQ2,-1.0]])],"derivedFrom":subQ1}),-1.0]])]});}
            var Q58;
            {var subQ0=sQuery(id+"F0.wireOp",EDGE,"E29.1.41");var subQ1=sQuery(id+"F0.wireOp",EDGE,"E12");var subQ2=makeQuery(id+"F0.imprint","INTERSECT",VERTEX,{"derivedFrom":[subQ1,subQ0]});Q58=makeQuery(id+"F0.imprint","IMPRINT",FACE,{"disambiguationData":[TD([[makeQuery(id+"F0.imprint","IMPRINT",EDGE,{"disambiguationData":[TD([[subQ2,-1.0]])],"derivedFrom":subQ1}),-1.0]])]});}
            extrude(context, id + "F2", {"entities" : qUnion([Q0, Q1, Q2, Q3, Q4, Q5, Q6, Q7, Q8, Q9, Q10, Q11, Q12, Q13, Q14, Q15, Q16, Q17, Q18, Q19, Q20, Q21, Q22, Q23, Q24, Q25, Q26, Q27, Q28, Q29, Q30, Q31, Q32, Q33, Q34, Q35, Q36, Q37, Q38, Q39, Q40, Q41, Q42, Q43, Q44, Q45, Q46, Q47, Q48, Q49, Q50, Q51, Q52, Q53, Q54, Q55, Q56, Q57, Q58]), "depth" : 2 * mm, "offsetDistance" : 25.4 * mm});
        }
        {
            var Q0;
            Q0=makeQuery(id+"F1.imprint","IMPRINT",FACE,{"disambiguationData":[TD([[makeQuery(id+"F1.imprint","IMPRINT",EDGE,{"derivedFrom":sQuery(id+"F1.wireOp",EDGE,"E30")}),1.0]])]});
            extrude(context, id + "F3", {"entities" : qUnion([Q0]), "operationType" : NewBodyOperationType.ADD, "depth" : 25.4 * mm, "offsetDistance" : 25.4 * mm});
        }
        {
            var Q0;
            Q0=qCreatedBy(makeId("Top.planeOp"),FACE);
            var sketch = newSketch(context, id + "F4", { "sketchPlane" : qUnion([Q0])});
            skFitSpline(sketch, "E31", {"points": [v(-29.87, 0.29) * mm, v(-29.34, 0.29) * mm, v(-28.46, 1.45) * mm, v(-26.9, 1.36) * mm, v(-25.63, 0.43) * mm, v(-25.25, 0) * mm, v(-24.99, -0.43) * mm, v(-25.5, -0.21) * mm, v(-26.25, 0) * mm, v(-27, -0.43) * mm, v(-28.3, -0.95) * mm, v(-29.34, 0) * mm, v(-29.94, 0) * mm, v(-29.87, 0.29) * mm]});
            skPoint(sketch, "E32", {"position": v(-27.65, 0.45) * mm});
            skSolve(sketch);
        }
        {
            var Q0;
            Q0=makeQuery(id+"F4.imprint","IMPRINT",FACE,{"disambiguationData":[TD([[makeQuery(id+"F4.imprint","IMPRINT",EDGE,{"derivedFrom":sQuery(id+"F4.wireOp",EDGE,"E31")}),-1.0]])]});
            extrude(context, id + "F5", {"entities" : qUnion([Q0]), "depth" : 1 * mm, "offsetDistance" : 25.4 * mm});
        }
        {
            var Q0;
            Q0=makeQuery(id+"F5.opExtrude","CAP_FACE",FACE,{"disambiguationData":[OSD([sQuery(id+"F4.wireOp",EDGE,"E31")])],"isStart":false});
            var sketch = newSketch(context, id + "F6", { "sketchPlane" : qUnion([Q0])});
            skPoint(sketch, "E33", {"position": v(-27.91, 0.45) * mm});
            skSolve(sketch);
        }
        {
            var Q0;
            Q0=makeQuery(id+"F5.opExtrude","SWEPT_BODY",BODY,{"disambiguationData":[OSD([sQuery(id+"F4.wireOp",EDGE,"E31")])]});
            var Q1;
            Q1=sQuery(id+"F6.wireOp",VERTEX,"E33");
            transform(context, id + "F7", {"entities" : qUnion([Q0]), "transformType" : TransformType.SCALE_UNIFORMLY, "scale" : 2.25, "scalePoint" : qUnion([Q1]), "makeCopy" : false});
        }
        {
            var Q0;
            Q0=makeQuery(id+"F5.opExtrude","SWEPT_BODY",BODY,{"disambiguationData":[OSD([sQuery(id+"F4.wireOp",EDGE,"E31")])]});
            transform(context, id + "F8", {"entities" : qUnion([Q0]), "transformType" : TransformType.TRANSLATION_3D, "dx" : 0 * mm, "dy" : 0 * mm, "dz" : 1 * mm, "makeCopy" : false});
        }
        {
            var Q0;
            Q0=qCreatedBy(makeId("Top.planeOp"),FACE);
            var sketch = newSketch(context, id + "F9", { "sketchPlane" : qUnion([Q0])});
            skCircle(sketch, "E34", {"center": v(-28.13, 0.3) * mm, "radius": 1.59 * mm});
            skSolve(sketch);
        }
        {
            var Q0;
            Q0=makeQuery(id+"F9.imprint","IMPRINT",FACE,{"disambiguationData":[TD([[makeQuery(id+"F9.imprint","IMPRINT",EDGE,{"derivedFrom":sQuery(id+"F9.wireOp",EDGE,"E34")}),1.0]])]});
            extrude(context, id + "F10", {"entities" : qUnion([Q0]), "operationType" : NewBodyOperationType.ADD, "depth" : 25.4 * mm, "offsetDistance" : 25.4 * mm});
        }
        {
            var Q0;
            Q0=qCreatedBy(makeId("Top.planeOp"),FACE);
            var sketch = newSketch(context, id + "F11", { "sketchPlane" : qUnion([Q0])});
            skFitSpline(sketch, "E35", {"points": [v(-32.88, -6.9) * mm, v(-31.44, -7.33) * mm, v(-30.9, -7.15) * mm, v(-28.14, -4.93) * mm, v(-21.12, -7.09) * mm, v(-18.06, -7.8) * mm, v(-18.06, -8.1) * mm, v(-21.06, -8.35) * mm, v(-27.54, -10.15) * mm, v(-30.78, -8.1) * mm, v(-31.44, -7.87) * mm, v(-32.82, -8.17) * mm, v(-32.88, -6.9) * mm]});
            skSolve(sketch);
        }
        {
            var Q0;
            Q0=qCreatedBy(makeId("Top.planeOp"),FACE);
            var sketch = newSketch(context, id + "F12", { "sketchPlane" : qUnion([Q0])});
            skCircle(sketch, "E36", {"center": v(-27.45, -7.39) * mm, "radius": 1.59 * mm});
            skSolve(sketch);
        }
        {
            var Q0;
            Q0=makeQuery(id+"F11.imprint","IMPRINT",FACE,{"disambiguationData":[TD([[makeQuery(id+"F11.imprint","IMPRINT",EDGE,{"derivedFrom":sQuery(id+"F11.wireOp",EDGE,"E35")}),-1.0]])]});
            extrude(context, id + "F13", {"entities" : qUnion([Q0]), "depth" : 2 * mm, "offsetDistance" : 25.4 * mm});
        }
        {
            var Q0;
            Q0 = qSketchRegion(id + "F12", true);
            extrude(context, id + "F14", {"entities" : qUnion([Q0]), "depth" : 25.4 * mm, "offsetDistance" : 25.4 * mm});
        }
    });
